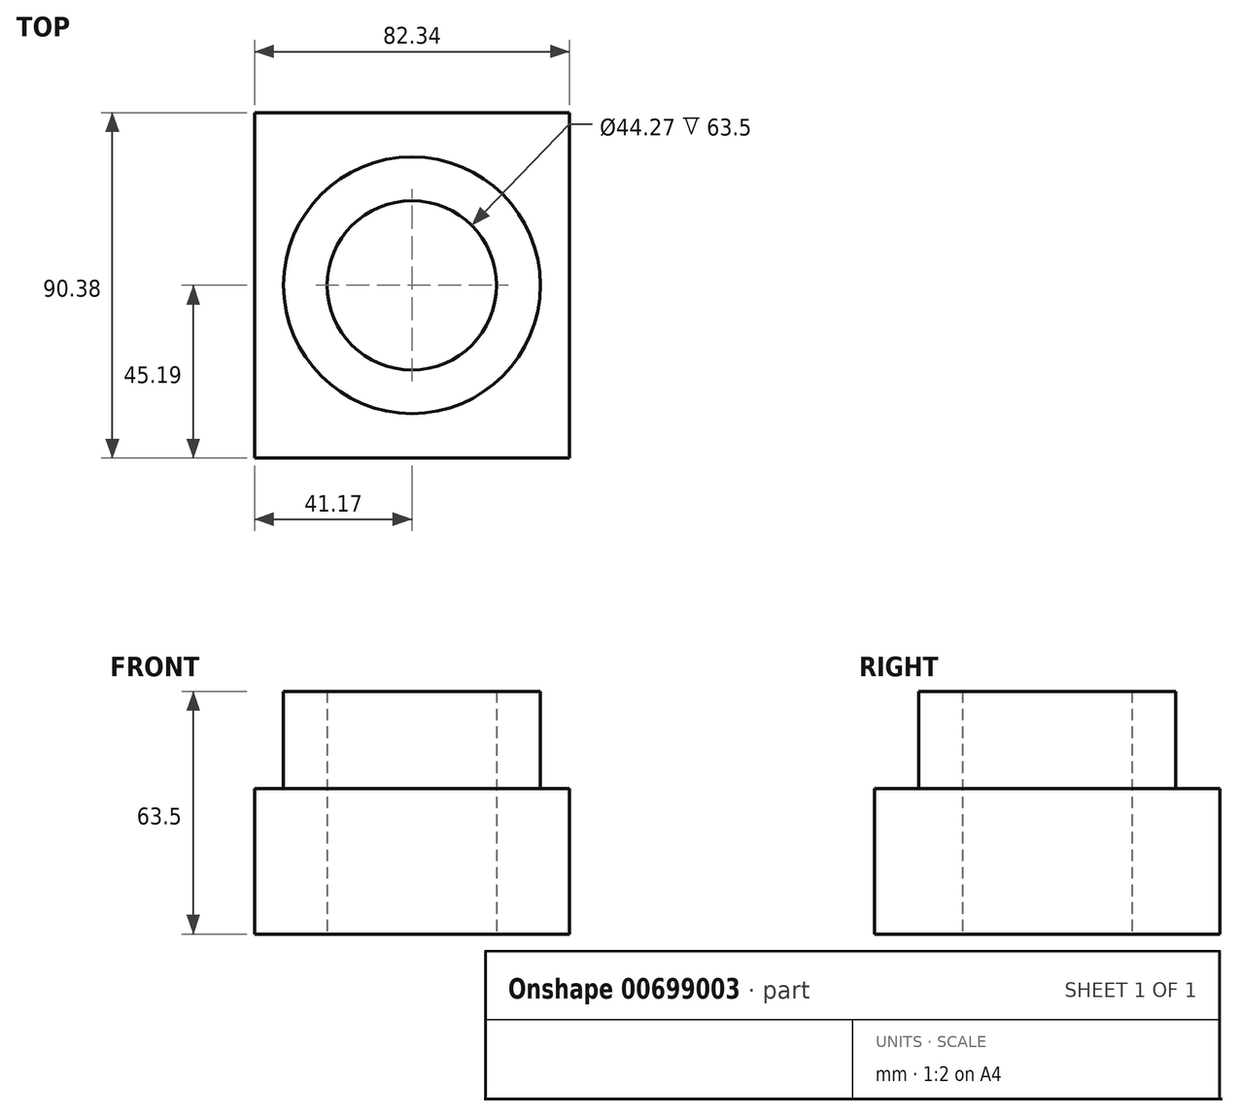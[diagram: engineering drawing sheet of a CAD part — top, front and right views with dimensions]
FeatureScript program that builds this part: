
annotation { "Feature Type Name" : "Feature", "Feature Type Description" : "" }
export const myFeature = defineFeature(function(context is Context, id is Id, definition is map)
    precondition{}
    {
        {
            var Q0;
            Q0=qCreatedBy(makeId("Top.planeOp"),FACE);
            var sketch = newSketch(context, id + "F0", { "sketchPlane" : qUnion([Q0])});
            skLineSegment(sketch, "E0.bottom", {"start": v(41.17, -45.19) * mm, "end": v(-41.17, -45.19) * mm});
            skLineSegment(sketch, "E0.top", {"start": v(41.17, 45.19) * mm, "end": v(-41.17, 45.19) * mm});
            skLineSegment(sketch, "E0.left", {"start": v(41.17, -45.19) * mm, "end": v(41.17, 45.19) * mm});
            skLineSegment(sketch, "E0.right", {"start": v(-41.17, -45.19) * mm, "end": v(-41.17, 45.19) * mm});
            skPoint(sketch, "E0.middle", {"position": v(0, 0) * mm});
            skSolve(sketch);
        }
        {
            var Q0;
            Q0=makeQuery(id+"F0.imprint","IMPRINT",FACE,{"disambiguationData":[TD([[makeQuery(id+"F0.imprint","IMPRINT",EDGE,{"derivedFrom":sQuery(id+"F0.wireOp",EDGE,"E0.bottom")}),-1.0]])]});
            extrude(context, id + "F1", {"entities" : qUnion([Q0]), "depth" : 38.1 * mm, "offsetDistance" : 25.4 * mm});
        }
        {
            var Q0;
            Q0=makeQuery(id+"F1.opExtrude","CAP_FACE",FACE,{"disambiguationData":[OSD([sQuery(id+"F0.wireOp",EDGE,"E0.bottom"),sQuery(id+"F0.wireOp",EDGE,"E0.top"),sQuery(id+"F0.wireOp",EDGE,"E0.left"),sQuery(id+"F0.wireOp",EDGE,"E0.right")])],"isStart":false});
            var sketch = newSketch(context, id + "F2", { "sketchPlane" : qUnion([Q0])});
            skCircle(sketch, "E1", {"center": v(0, 0) * mm, "radius": 22.13 * mm});
            skCircle(sketch, "E2", {"center": v(0, 0) * mm, "radius": 33.56 * mm});
            skSolve(sketch);
        }
        {
            var Q0;
            Q0=makeQuery(id+"F2.imprint","IMPRINT",FACE,{"disambiguationData":[TD([[makeQuery(id+"F2.imprint","IMPRINT",EDGE,{"derivedFrom":sQuery(id+"F2.wireOp",EDGE,"E1")}),-1.0]])]});
            extrude(context, id + "F3", {"entities" : qUnion([Q0]), "operationType" : NewBodyOperationType.ADD, "depth" : 25.4 * mm, "offsetDistance" : 25.4 * mm});
        }
        {
            var Q0;
            Q0=makeQuery(id+"F3.boolean.opBoolean","SPLIT",FACE,{"disambiguationData":[TD([makeQuery(id+"F3.opExtrude","SWEPT_FACE",FACE,{"disambiguationData":[OSD([sQuery(id+"F2.wireOp",EDGE,"E1")])]})])],"derivedFrom":makeQuery(id+"F1.opExtrude","CAP_FACE",FACE,{"disambiguationData":[OSD([sQuery(id+"F0.wireOp",EDGE,"E0.bottom"),sQuery(id+"F0.wireOp",EDGE,"E0.top"),sQuery(id+"F0.wireOp",EDGE,"E0.left"),sQuery(id+"F0.wireOp",EDGE,"E0.right")])],"isStart":false})});
            extrude(context, id + "F4", {"entities" : qUnion([Q0]), "operationType" : NewBodyOperationType.REMOVE, "oppositeDirection" : true, "depth" : 127 * mm, "offsetDistance" : 25.4 * mm});
        }
    });
